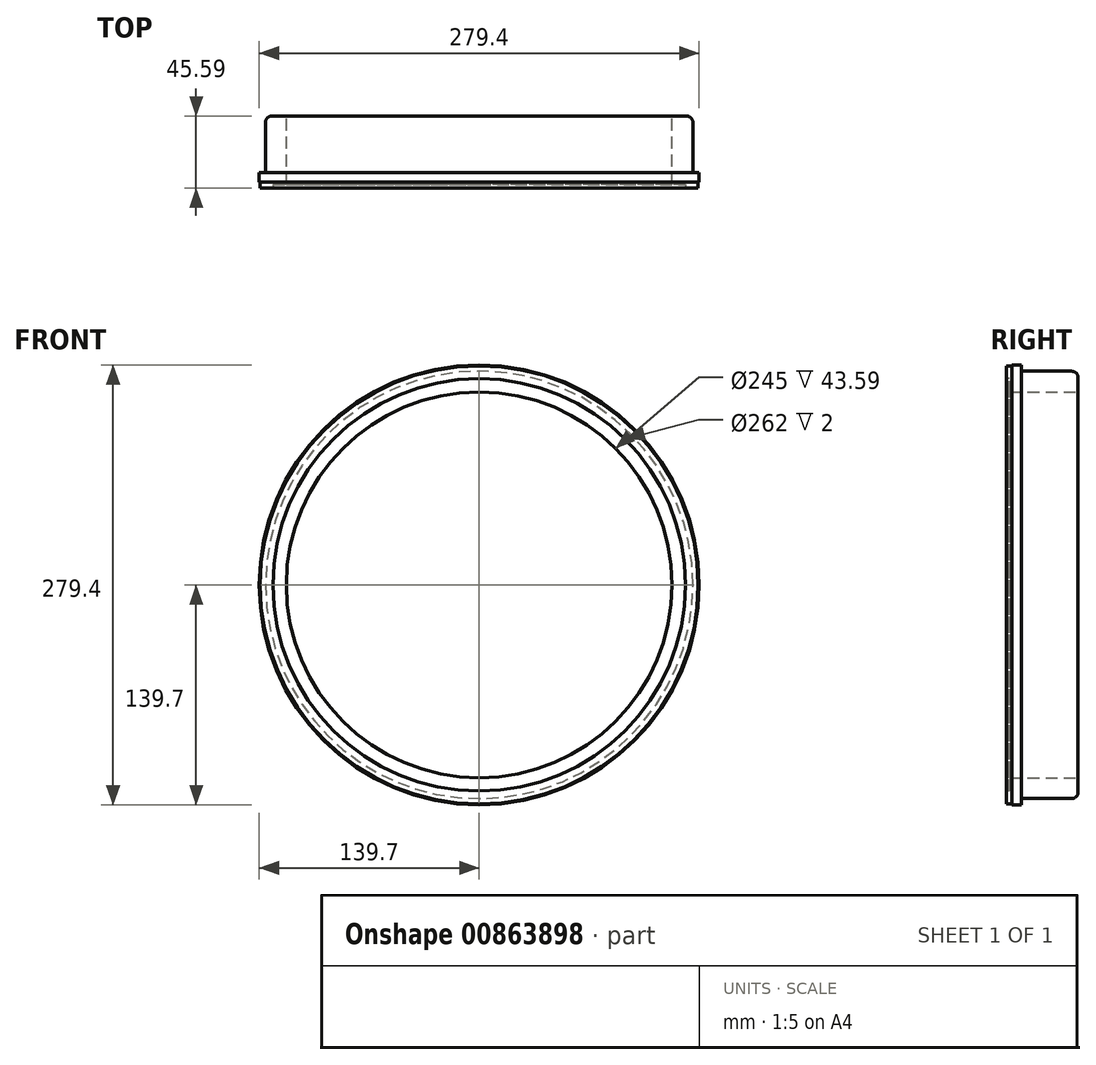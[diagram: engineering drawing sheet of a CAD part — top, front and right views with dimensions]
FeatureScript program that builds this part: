
annotation { "Feature Type Name" : "Feature", "Feature Type Description" : "" }
export const myFeature = defineFeature(function(context is Context, id is Id, definition is map)
    precondition{}
    {
        {
            var Q0;
            Q0=qCreatedBy(makeId("Front.planeOp"),FACE);
            var sketch = newSketch(context, id + "F0", { "sketchPlane" : qUnion([Q0])});
            skCircle(sketch, "E0", {"center": v(0, 0) * mm, "radius": 139.7 * mm});
            skCircle(sketch, "E1", {"center": v(0, 0) * mm, "radius": 122.5 * mm});
            skSolve(sketch);
        }
        {
            var Q0;
            Q0=makeQuery(id+"F0.imprint","IMPRINT",FACE,{"disambiguationData":[TD([[makeQuery(id+"F0.imprint","IMPRINT",EDGE,{"derivedFrom":sQuery(id+"F0.wireOp",EDGE,"E0")}),1.0]])]});
            extrude(context, id + "F1", {"entities" : qUnion([Q0]), "depth" : 6 * mm, "offsetDistance" : 25 * mm});
        }
        {
            var Q0;
            Q0=makeQuery(id+"F1.opExtrude","CAP_FACE",FACE,{"disambiguationData":[OSD([sQuery(id+"F0.wireOp",EDGE,"E0"),sQuery(id+"F0.wireOp",EDGE,"E1")])],"isStart":false});
            var sketch = newSketch(context, id + "F2", { "sketchPlane" : qUnion([Q0])});
            skCircle(sketch, "E2", {"center": v(0, 0) * mm, "radius": 139.1 * mm});
            skCircle(sketch, "E3", {"center": v(0, 0) * mm, "radius": 122.5 * mm});
            skSolve(sketch);
        }
        {
            var Q0;
            Q0=makeQuery(id+"F2.imprint","IMPRINT",FACE,{"disambiguationData":[TD([[makeQuery(id+"F2.imprint","IMPRINT",EDGE,{"derivedFrom":sQuery(id+"F2.wireOp",EDGE,"E2")}),1.0]])]});
            extrude(context, id + "F3", {"entities" : qUnion([Q0]), "operationType" : NewBodyOperationType.ADD, "depth" : 3.59 * mm, "offsetDistance" : 25 * mm});
        }
        {
            var Q0;
            Q0=makeQuery(id+"F1.opExtrude","CAP_FACE",FACE,{"disambiguationData":[OSD([sQuery(id+"F0.wireOp",EDGE,"E0"),sQuery(id+"F0.wireOp",EDGE,"E1")])],"isStart":true});
            var sketch = newSketch(context, id + "F4", { "sketchPlane" : qUnion([Q0])});
            skCircle(sketch, "E4", {"center": v(0, 0) * mm, "radius": 135.7 * mm});
            skCircle(sketch, "E5", {"center": v(0, 0) * mm, "radius": 122.5 * mm});
            skSolve(sketch);
        }
        {
            var Q0;
            Q0=makeQuery(id+"F4.imprint","IMPRINT",FACE,{"disambiguationData":[TD([[makeQuery(id+"F4.imprint","IMPRINT",EDGE,{"derivedFrom":sQuery(id+"F4.wireOp",EDGE,"E4")}),1.0]])]});
            extrude(context, id + "F5", {"entities" : qUnion([Q0]), "operationType" : NewBodyOperationType.ADD, "depth" : 36 * mm, "offsetDistance" : 25 * mm});
        }
        {
            var Q0;
            Q0=makeQuery(id+"F3.opExtrude","CAP_FACE",FACE,{"disambiguationData":[OSD([sQuery(id+"F2.wireOp",EDGE,"E2"),sQuery(id+"F2.wireOp",EDGE,"E3")])],"isStart":false});
            var sketch = newSketch(context, id + "F6", { "sketchPlane" : qUnion([Q0])});
            skCircle(sketch, "E6", {"center": v(0, 0) * mm, "radius": 122.5 * mm});
            skCircle(sketch, "E7", {"center": v(0, 0) * mm, "radius": 131 * mm});
            skSolve(sketch);
        }
        {
            var Q0;
            Q0=makeQuery(id+"F6.imprint","IMPRINT",FACE,{"disambiguationData":[TD([[makeQuery(id+"F6.imprint","IMPRINT",EDGE,{"derivedFrom":sQuery(id+"F6.wireOp",EDGE,"E6")}),-1.0]])]});
            extrude(context, id + "F7", {"entities" : qUnion([Q0]), "operationType" : NewBodyOperationType.REMOVE, "oppositeDirection" : true, "depth" : 2 * mm, "offsetDistance" : 25 * mm});
        }
        {
            var Q0;
            Q0=makeQuery(id+"F5.opExtrude","CAP_EDGE",EDGE,{"disambiguationData":[OSD([sQuery(id+"F4.wireOp",EDGE,"E4")])],"isStart":false});
            fillet(context, id + "F8", {"entities" : qUnion([Q0]), "radius" : 4 * mm, "tangentPropagation" : true, "allowEdgeOverflow" : false});
        }
    });
